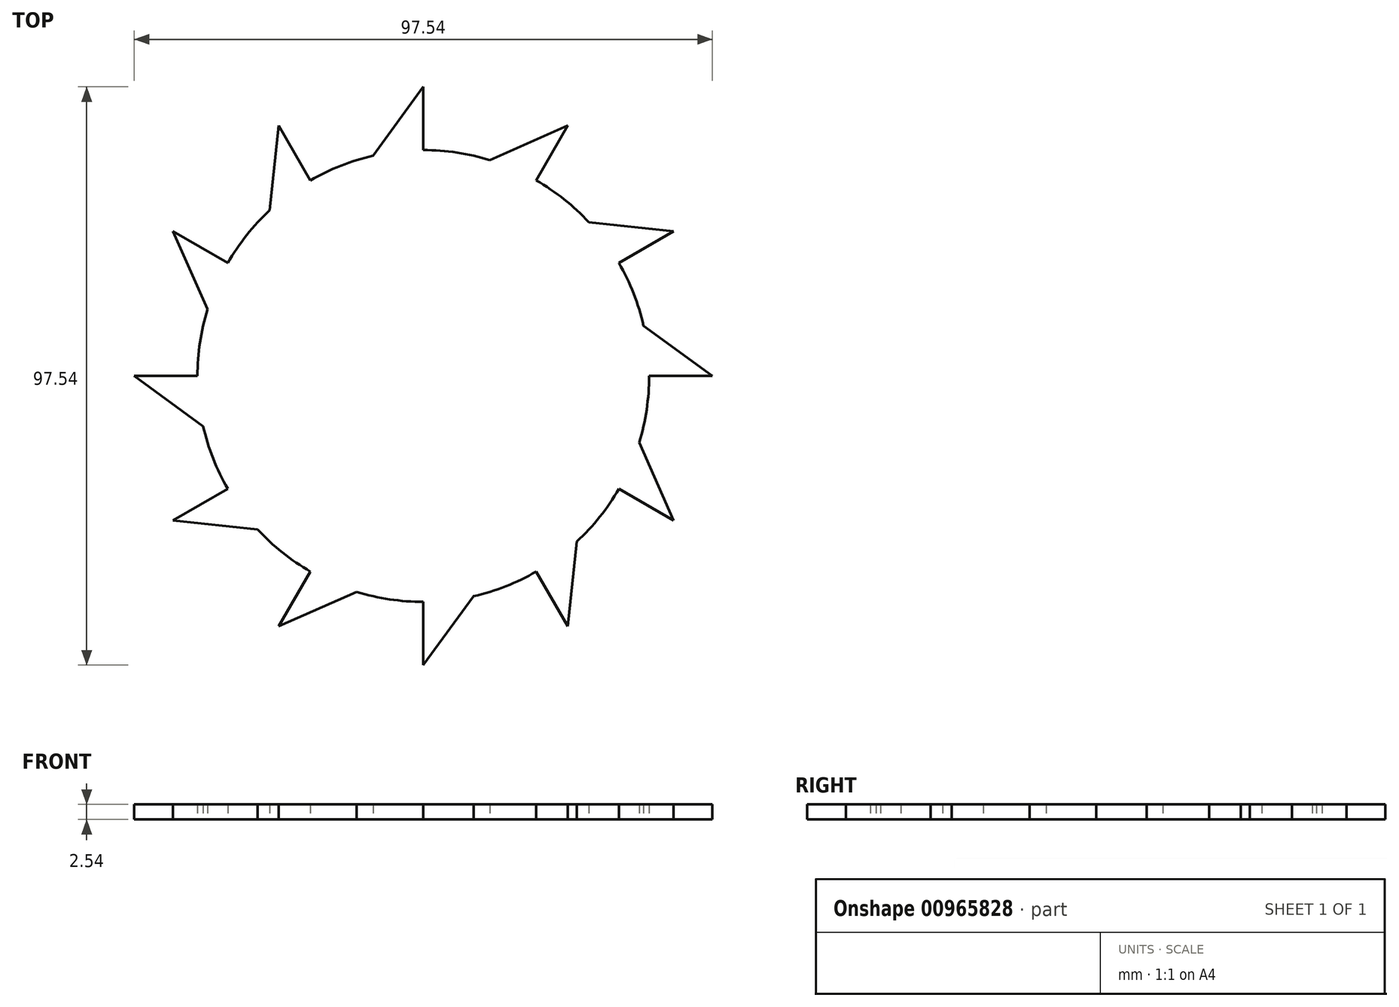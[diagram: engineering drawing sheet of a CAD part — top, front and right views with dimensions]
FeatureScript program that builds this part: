
annotation { "Feature Type Name" : "Feature", "Feature Type Description" : "" }
export const myFeature = defineFeature(function(context is Context, id is Id, definition is map)
    precondition{}
    {
        {
            var Q0;
            Q0=qCreatedBy(makeId("Top.planeOp"),FACE);
            var sketch = newSketch(context, id + "F0", { "sketchPlane" : qUnion([Q0])});
            skCircle(sketch, "E0", {"center": v(0, 0) * mm, "radius": 38.1 * mm});
            skLineSegment(sketch, "E1", {"start": v(0, 38.1) * mm, "end": v(0, 48.77) * mm});
            skLineSegment(sketch, "E2", {"start": v(0, 48.77) * mm, "end": v(-8.47, 37.15) * mm});
            skPoint(sketch, "E3.MirrorCS.end.orphan", {"position": v(0, 48.77) * mm});
            skPoint(sketch, "E3.MirrorCS.start.orphan", {"position": v(-10.15, 45.5) * mm});
            skLineSegment(sketch, "E4.1.0", {"start": v(-24.38, 42.23) * mm, "end": v(-25.9, 27.93) * mm});
            skLineSegment(sketch, "E4.1.1", {"start": v(-19.05, 33) * mm, "end": v(-24.38, 42.23) * mm});
            skLineSegment(sketch, "E4.2.0", {"start": v(-42.23, 24.38) * mm, "end": v(-36.4, 11.24) * mm});
            skLineSegment(sketch, "E4.2.1", {"start": v(-33, 19.05) * mm, "end": v(-42.23, 24.38) * mm});
            skLineSegment(sketch, "E4.3.0", {"start": v(-48.77, 0) * mm, "end": v(-37.15, -8.47) * mm});
            skLineSegment(sketch, "E4.3.1", {"start": v(-38.1, 0) * mm, "end": v(-48.77, 0) * mm});
            skLineSegment(sketch, "E4.4.0", {"start": v(-42.23, -24.38) * mm, "end": v(-27.93, -25.9) * mm});
            skLineSegment(sketch, "E4.4.1", {"start": v(-33, -19.05) * mm, "end": v(-42.23, -24.38) * mm});
            skLineSegment(sketch, "E4.5.0", {"start": v(-24.38, -42.23) * mm, "end": v(-11.24, -36.4) * mm});
            skLineSegment(sketch, "E4.5.1", {"start": v(-19.05, -33) * mm, "end": v(-24.38, -42.23) * mm});
            skLineSegment(sketch, "E4.6.0", {"start": v(0, -48.77) * mm, "end": v(8.47, -37.15) * mm});
            skLineSegment(sketch, "E4.6.1", {"start": v(0, -38.1) * mm, "end": v(0, -48.77) * mm});
            skLineSegment(sketch, "E4.7.0", {"start": v(24.38, -42.23) * mm, "end": v(25.9, -27.93) * mm});
            skLineSegment(sketch, "E4.7.1", {"start": v(19.05, -33) * mm, "end": v(24.38, -42.23) * mm});
            skLineSegment(sketch, "E4.8.0", {"start": v(42.23, -24.38) * mm, "end": v(36.4, -11.24) * mm});
            skLineSegment(sketch, "E4.8.1", {"start": v(33, -19.05) * mm, "end": v(42.23, -24.38) * mm});
            skLineSegment(sketch, "E4.9.0", {"start": v(48.77, 0) * mm, "end": v(37.15, 8.47) * mm});
            skLineSegment(sketch, "E4.9.1", {"start": v(38.1, 0) * mm, "end": v(48.77, 0) * mm});
            skLineSegment(sketch, "E4.10.0", {"start": v(42.23, 24.38) * mm, "end": v(27.93, 25.9) * mm});
            skLineSegment(sketch, "E4.10.1", {"start": v(33, 19.05) * mm, "end": v(42.23, 24.38) * mm});
            skLineSegment(sketch, "E4.11.0", {"start": v(24.38, 42.23) * mm, "end": v(11.24, 36.4) * mm});
            skLineSegment(sketch, "E4.11.1", {"start": v(19.05, 33) * mm, "end": v(24.38, 42.23) * mm});
            skSolve(sketch);
        }
        {
            var Q0;
            Q0 = qSketchRegion(id + "F0", true);
            extrude(context, id + "F1", {"entities" : qUnion([Q0]), "depth" : 2.54 * mm, "offsetDistance" : 25.4 * mm});
        }
    });
